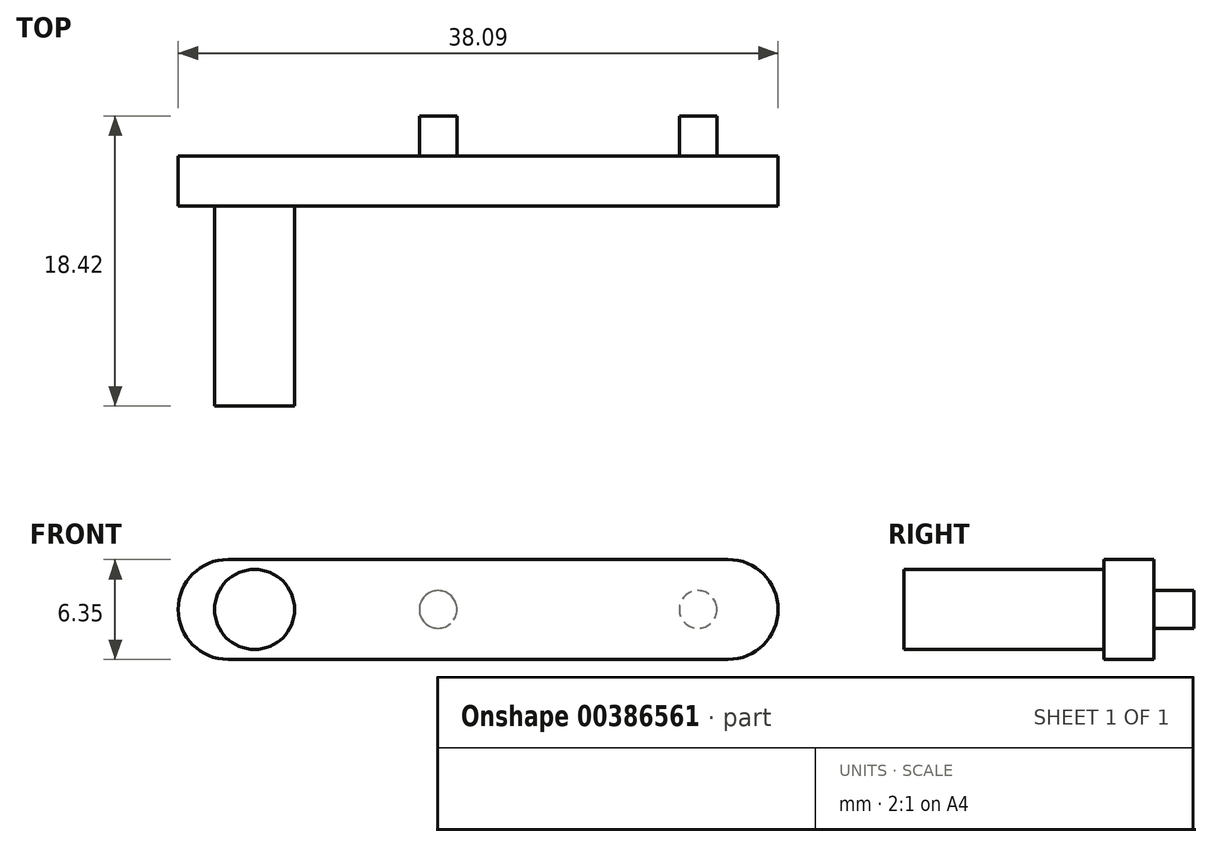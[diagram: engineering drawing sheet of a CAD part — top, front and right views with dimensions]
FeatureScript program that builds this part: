
annotation { "Feature Type Name" : "Feature", "Feature Type Description" : "" }
export const myFeature = defineFeature(function(context is Context, id is Id, definition is map)
    precondition{}
    {
        {
            var Q0;
            Q0=qCreatedBy(makeId("Front.planeOp"),FACE);
            var sketch = newSketch(context, id + "F0", { "sketchPlane" : qUnion([Q0])});
            skArc(sketch, "E0", {"start": v(0, 3.18) * mm, "mid": v(-3.18, 0) * mm, "end": v(0, -3.18) * mm});
            skArc(sketch, "E1", {"start": v(31.75, -3.17) * mm, "mid": v(34.93, 0) * mm, "end": v(31.75, 3.18) * mm});
            skLineSegment(sketch, "E2", {"start": v(0, 3.18) * mm, "end": v(31.75, 3.18) * mm});
            skLineSegment(sketch, "E3", {"start": v(0, -3.18) * mm, "end": v(31.75, -3.18) * mm});
            skSolve(sketch);
        }
        {
            var Q0;
            Q0=makeQuery(id+"F0.imprint","IMPRINT",FACE,{"disambiguationData":[TD([[makeQuery(id+"F0.imprint","IMPRINT",EDGE,{"derivedFrom":sQuery(id+"F0.wireOp",EDGE,"E0")}),1.0]])]});
            extrude(context, id + "F1", {"entities" : qUnion([Q0]), "depth" : 3.17 * mm});
        }
        {
            var Q0;
            Q0=makeQuery(id+"F1.opExtrude","CAP_FACE",FACE,{"disambiguationData":[OSD([sQuery(id+"F0.wireOp",EDGE,"E0"),sQuery(id+"F0.wireOp",EDGE,"E1"),sQuery(id+"F0.wireOp",EDGE,"E2"),sQuery(id+"F0.wireOp",EDGE,"E3")])],"isStart":false});
            var sketch = newSketch(context, id + "F2", { "sketchPlane" : qUnion([Q0])});
            skCircle(sketch, "E4", {"center": v(1.68, 0) * mm, "radius": 2.54 * mm});
            skSolve(sketch);
        }
        {
            var Q0;
            Q0 = qSketchRegion(id + "F2", true);
            extrude(context, id + "F3", {"entities" : qUnion([Q0]), "operationType" : NewBodyOperationType.ADD, "depth" : 12.7 * mm});
        }
        {
            var Q0;
            Q0=makeQuery(id+"F1.opExtrude","CAP_FACE",FACE,{"disambiguationData":[OSD([sQuery(id+"F0.wireOp",EDGE,"E0"),sQuery(id+"F0.wireOp",EDGE,"E1"),sQuery(id+"F0.wireOp",EDGE,"E2"),sQuery(id+"F0.wireOp",EDGE,"E3")])],"isStart":true});
            var sketch = newSketch(context, id + "F4", { "sketchPlane" : qUnion([Q0])});
            skCircle(sketch, "E5", {"center": v(-29.85, 0) * mm, "radius": 1.2 * mm});
            skCircle(sketch, "E6", {"center": v(-13.34, 0) * mm, "radius": 1.2 * mm});
            skSolve(sketch);
        }
        {
            var Q0;
            Q0 = qSketchRegion(id + "F4", true);
            extrude(context, id + "F5", {"entities" : qUnion([Q0]), "operationType" : NewBodyOperationType.ADD, "depth" : 2.54 * mm});
        }
    });
